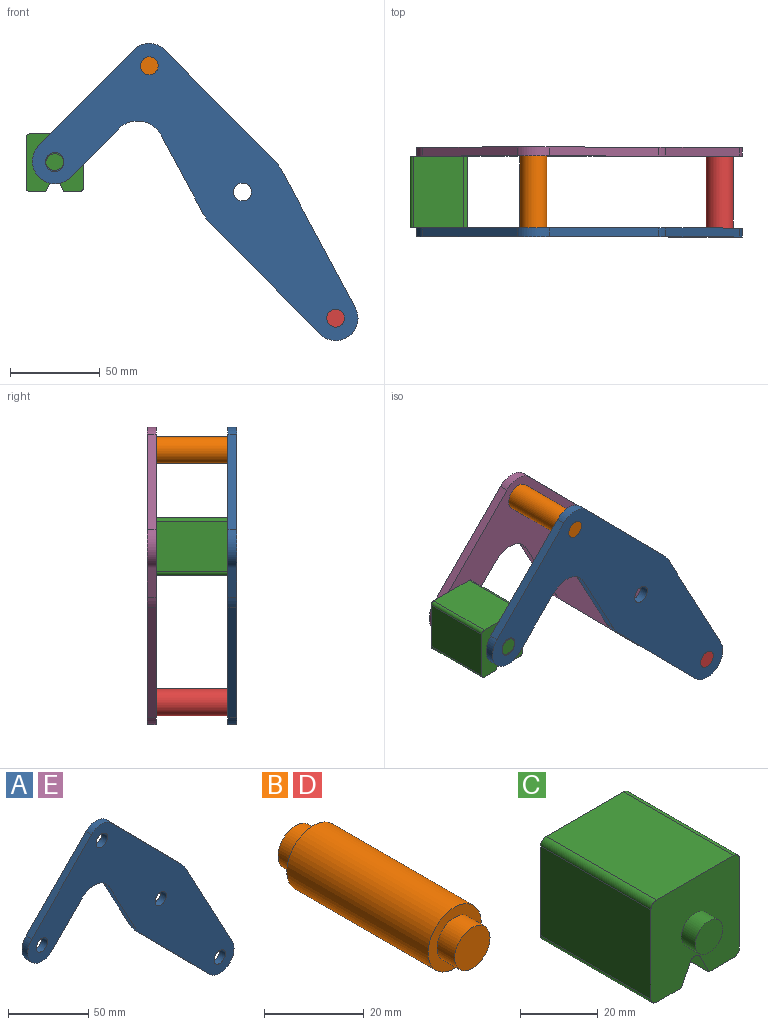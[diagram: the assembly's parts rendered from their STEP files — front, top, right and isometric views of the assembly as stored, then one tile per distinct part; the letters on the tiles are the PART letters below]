
ASSEMBLY  parts=5 mates=3
PART A: 18 faces, bbox 181.7x5x165.8 mm
  f0: plane 43.49x23.35mm, normal (-0.88,0,-0.47), area 246.8mm2, adj f1,f14,f16,f17
  f1: cylinder r=25mm len=5.75mm, axis (0,1,0), area 35.8mm2, adj f0,f2,f16,f17
  f2: plane 61.6x60.87mm, normal (-0.71,0,-0.7), area 433mm2, adj f1,f3,f16,f17
  f3: cylinder r=12.5mm len=21.39mm, axis (0,1,0), area 178.4mm2, adj f2,f4,f16,f17
  f4: plane 76.3x40.96mm, normal (0.88,0,0.47), area 433mm2, adj f3,f5,f16,f17
  f5: cylinder r=25mm len=5.75mm, axis (0,1,0), area 35.8mm2, adj f4,f6,f16,f17
  f6: plane 61.6x60.87mm, normal (0.71,0,0.7), area 433mm2, adj f5,f7,f16,f17
  f7: cylinder r=12.5mm len=17.78mm, axis (0,1,0), area 98.9mm2, adj f6,f8,f16,f17
  f8: plane 53.35x52.71mm, normal (-0.71,0,0.7), area 375mm2, adj f7,f9,f16,f17
  f9: cylinder r=12.5mm len=21.39mm, axis (0,1,0), area 196.3mm2, adj f8,f10,f16,f17
  f10: plane 26.86x26.54mm, normal (0.71,0,-0.7), area 188.8mm2, adj f9,f14,f16,f17
  f11: cylinder r=5mm len=10mm, axis (0,1,0), area 157.1mm2, adj f16,f17
  f12: cylinder r=5mm len=10mm, axis (0,1,0), area 157.1mm2, adj f16,f17
  f13: cylinder r=5mm len=10mm, axis (0,1,0), area 157.1mm2, adj f16,f17
  f14: cylinder r=15mm len=23.89mm, axis (0,1,0), area 140.2mm2, adj f0,f10,f16,f17
  f15: cylinder r=5mm len=10mm, axis (0,1,0), area 157.1mm2, adj f16,f17
  f16: plane 181.66x165.78mm, normal (0,-1,0), area 8710.1mm2, adj f0,f1,f2,f3,f4,f5,f6,f7
  f17: plane 181.66x165.78mm, normal (0,1,0), area 8710.1mm2, adj f0,f1,f2,f3,f4,f5,f6,f7
PART B: 7 faces, bbox 15x50x15 mm
  f0: cylinder r=7.5mm len=40mm, axis (0,-1,0), area 1885mm2, adj f2,f5
  f1: cylinder r=5mm len=10mm, axis (0,1,0), area 157.1mm2, adj f2,f3
  f2: plane 15x15mm, normal (0,-1,0), area 98.2mm2, adj f0,f1
  f3: plane 10x10mm, normal (0,-1,0), area 78.5mm2, adj f1
  f4: cylinder r=5mm len=10mm, axis (0,-1,0), area 157.1mm2, adj f5,f6
  f5: plane 15x15mm, normal (0,1,0), area 98.2mm2, adj f0,f4
  f6: plane 10x10mm, normal (0,1,0), area 78.5mm2, adj f4
PART C: 18 faces, bbox 32.1x50x32.1 mm
  f0: plane 40x28.08mm, normal (1,0,0), area 1123.1mm2, adj f4,f10,f13,f14
  f1: plane 40x9.04mm, normal (0,0,-1), area 361.6mm2, adj f2,f4,f10,f14
  f2: plane 40x6.42mm, normal (-0.89,0,-0.45), area 287.2mm2, adj f1,f4,f10,f15
  f3: plane 40x6.42mm, normal (0.89,0,-0.45), area 287.2mm2, adj f4,f5,f10,f15
  f4: plane 32.08x32.08mm, normal (0,-1,0), area 900.6mm2, adj f0,f1,f2,f3,f5,f6,f7,f9
  f5: plane 40x9.04mm, normal (0,0,-1), area 361.6mm2, adj f3,f4,f10,f16
  f6: plane 40x28.08mm, normal (0,0,1), area 1123.1mm2, adj f4,f10,f13,f17
  f7: plane 40x28.08mm, normal (-1,0,0), area 1123.1mm2, adj f4,f10,f16,f17
  f8: plane 10x10mm, normal (0,-1,0), area 78.5mm2, adj f9
  f9: cylinder r=5mm len=10mm, axis (0,1,0), area 157.1mm2, adj f4,f8
  f10: plane 32.08x32.08mm, normal (0,1,0), area 900.6mm2, adj f0,f1,f2,f3,f5,f6,f7,f12
  f11: plane 10x10mm, normal (0,1,0), area 78.5mm2, adj f12
  f12: cylinder r=5mm len=10mm, axis (0,-1,0), area 157.1mm2, adj f10,f11
  f13: cylinder r=2mm len=40mm, axis (0,1,0), area 125.7mm2, adj f0,f4,f6,f10
  f14: cylinder r=2mm len=40mm, axis (0,-1,0), area 125.7mm2, adj f0,f1,f4,f10
  f15: cylinder r=2mm len=40mm, axis (0,1,0), area 177.1mm2, adj f2,f3,f4,f10
  f16: cylinder r=2mm len=40mm, axis (0,1,0), area 125.7mm2, adj f4,f5,f7,f10
  f17: cylinder r=2mm len=40mm, axis (0,-1,0), area 125.7mm2, adj f4,f6,f7,f10
PART D: same geometry as B
PART E: same geometry as A
PLACE A t=(0,-20,0)mm fixed
PLACE B t=(0,-20,0)mm
PLACE C t=(0,-20,-0.67)mm
PLACE D t=(103.95,-20,-140.78)mm
PLACE E t=(0,25,0)mm
MATE fastened A.f3 <-> D.f0  axis (0,1,0) through (51.98,-20,-70.39)mm
MATE fastened E.f7 <-> B.f0  axis (0,-1,0) through (-51.98,20,70.39)mm
MATE revolute A.f9 <-> C.f4  axis (0,1,0) through (-104.69,-20,17.04)mm
